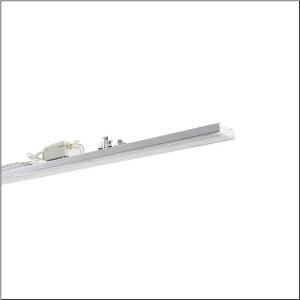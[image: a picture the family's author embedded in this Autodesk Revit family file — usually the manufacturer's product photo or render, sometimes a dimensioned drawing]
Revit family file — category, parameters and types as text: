
# Revit family: licross_r__21_recessed_mo_52te12dn4axg3s4_eb36
name_source: partatom
category: Lighting Fixtures
units: mm (PartAtom-declared; Revit-internal decimal feet)

## family parameters
Cut with Voids When Loaded = No
Host = Face
Light Source = No
Part Type = Normal
Room Calculation Point = No
Round Connector Dimension = Use Diameter
Shared = No

## types (1)
- --- (1 x LED, 950 lm, 6.7 W, 4000K)
    Apparent Load = 7 VA
    CIE Flux Codes = 72 92 99 100 100
    Color Rendering = 80
    Color Temperature = 4000K
    Default Elevation = 1800 mm
    Description = Licross® 21 Recessed MO, luminaire insert, of sheet steel, galvanised, coil coated, white, length: 1.500mm, width: 66mm, height: 67mm, LED rated luminous flux: 10.280lm, light colour: 840, control gear: DALI 2, with plug, 6-pole, with phase selection, for trunking rail, 9 or 11-core, mains connection: 220..240V, AC, 50/60Hz, rated input power: 62W, halogen-free wiring, for emergency light function, for trunking rail, 9-/11-core, converter,control gear: single battery element, battery: LiFeP04, 9Ah, primary optical cover: cover, of PMMA, light emission: direct distribution, primary light characteristic: symmetric, protection rating (complete): IP54, insulation class (complete): insulation class I (protective earthing), certification: CE, UKCA, protection symbol: D if used in an environment with non-conductive dust loads with corresponding accessories, impact resistance: IK06, permissible ambient temperature for indoor applications: +5..+35°C, standard: EN 60598-2-22, LABS conformity tested according to VDMA 24364:2018-05, reducing of maximum allowable ambient temperature of 5°C with ceiling mounting, corresponds to IFS (International Featured Standards) requirements for safety and quality in the food industry, packaging unit: 1 piece
    Height = 58 mm
    Lamp = 1 x LED
    Lamp Light Flux = 950 lm
    Lamp Power = 6.7 W
    Lamp count = 1
    Length = 1500 mm
    Luminous efficacy = 142 lm/W
    Manufacturer = Siteco
    ModVariant = No
    Model = 52TE12DN4AXG3S4
    Mounting Place = Ceiling
    Mounting Type = Pendant
    Number of Poles = 1
    OnlyDefault = Yes
    Power Factor = 1
    Product Name = Licross® 21 Recessed MO
    Product group = luminaire insert
    ProductGroupID = 901
    Protection Class = Protection class I
    Protection Degree = IP 54
    RLX_Detail_Level = 1
    RLX_Emergency_Light_Flux = 0 lm
    RLX_Emergency_Type = 0
    RLX_Emergency_Type_DB = No
    RlxData = <blob elided: 25021 chars, md5=959ec95e>
    Socket = socket
    Standby Power = 0 W
    System Light Flux = 950 lm
    System Power = 7 W
    Type Comments = : emergency light operation: 3 h
    Type Image = l_1296930.jpg
    URL = http://relux.com
    VarID = @adj_040177
    Voltage = 0 V
    Weight = 0.00 kg
    Width = 66 mm

## geometry (parser evidence)
native form markers: Blend x4, Sweep x11
no freeform markers — native parametric forms only
